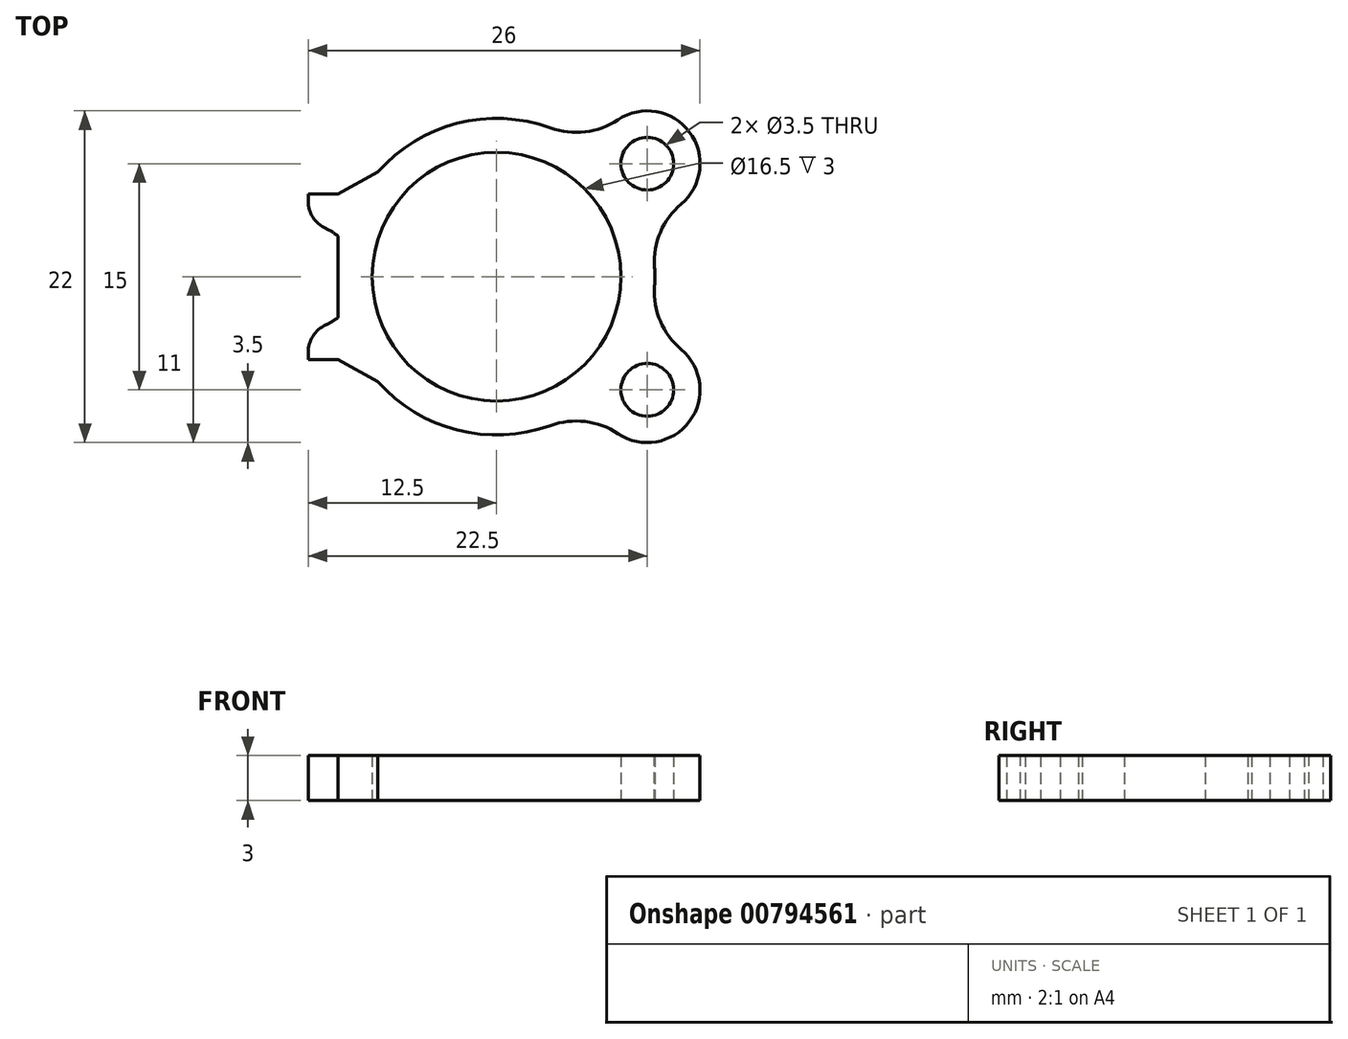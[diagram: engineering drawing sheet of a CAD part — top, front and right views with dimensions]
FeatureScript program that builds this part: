
annotation { "Feature Type Name" : "Feature", "Feature Type Description" : "" }
export const myFeature = defineFeature(function(context is Context, id is Id, definition is map)
    precondition{}
    {
        {
            var Q0;
            Q0=qCreatedBy(makeId("Top.planeOp"),FACE);
            var sketch = newSketch(context, id + "F0", { "sketchPlane" : qUnion([Q0])});
            skCircle(sketch, "E0", {"center": v(0, 0) * mm, "radius": 10.5 * mm});
            skCircle(sketch, "E1", {"center": v(0, 0) * mm, "radius": 8.25 * mm});
            skCircle(sketch, "E2", {"center": v(10, 7.5) * mm, "radius": 1.75 * mm});
            skCircle(sketch, "E3", {"center": v(10, -7.5) * mm, "radius": 1.75 * mm});
            skCircle(sketch, "E4", {"center": v(10, 7.5) * mm, "radius": 3.5 * mm});
            skCircle(sketch, "E5", {"center": v(10, -7.5) * mm, "radius": 3.5 * mm});
            skLineSegment(sketch, "E6", {"start": v(-12.5, 5.5) * mm, "end": v(-12.5, -5.5) * mm});
            skLineSegment(sketch, "E7", {"start": v(-12.5, -5.5) * mm, "end": v(-10.5, -5.5) * mm});
            skLineSegment(sketch, "E8", {"start": v(-12.5, 5.5) * mm, "end": v(-10.5, 5.5) * mm});
            skLineSegment(sketch, "E9", {"start": v(-10.5, 5.5) * mm, "end": v(-10.5, -5.5) * mm});
            skLineSegment(sketch, "E10", {"start": v(-10.5, 5.5) * mm, "end": v(-7.87, 6.95) * mm});
            skLineSegment(sketch, "E11", {"start": v(-10.5, -5.5) * mm, "end": v(-7.87, -6.95) * mm});
            skCircle(sketch, "E12", {"center": v(0, 0) * mm, "radius": 9.25 * mm});
            skLineSegment(sketch, "E13", {"start": v(-7.87, 6.95) * mm, "end": v(-7.23, 5.77) * mm});
            skLineSegment(sketch, "E14", {"start": v(-7.87, -6.95) * mm, "end": v(-7.23, -5.77) * mm});
            skCircle(sketch, "E15", {"center": v(-12.75, 0) * mm, "radius": 1.75 * mm});
            skCircle(sketch, "E16", {"center": v(-12.75, 0) * mm, "radius": 3.5 * mm});
            skSolve(sketch);
        }
        {
            var Q0;
            {var subQ2=sQuery(id+"F0.wireOp",EDGE,"E16");var subQ5=sQuery(id+"F0.wireOp",EDGE,"E6");var subQ9=makeQuery(id+"F0.imprint","INTERSECT",VERTEX,{"disambiguationData":[OD(0.0)],"derivedFrom":[subQ5,subQ2]});Q0=makeQuery(id+"F0.imprint","IMPRINT",FACE,{"disambiguationData":[TD([[makeQuery(id+"F0.imprint","IMPRINT",EDGE,{"disambiguationData":[TD([[subQ9,-1.0]])],"derivedFrom":subQ5}),1.0]])]});}
            var Q1;
            {var subQ0=sQuery(id+"F0.wireOp",EDGE,"E16");var subQ1=sQuery(id+"F0.wireOp",EDGE,"E6");var subQ2=makeQuery(id+"F0.imprint","INTERSECT",VERTEX,{"disambiguationData":[OD(0.0)],"derivedFrom":[subQ1,subQ0]});Q1=makeQuery(id+"F0.imprint","IMPRINT",FACE,{"disambiguationData":[TD([[makeQuery(id+"F0.imprint","IMPRINT",EDGE,{"disambiguationData":[TD([[subQ2,-1.0]])],"derivedFrom":subQ1}),-1.0]])]});}
            var Q2;
            {var subQ0=sQuery(id+"F0.wireOp",EDGE,"E8");Q2=makeQuery(id+"F0.imprint","IMPRINT",FACE,{"disambiguationData":[TD([[makeQuery(id+"F0.imprint","IMPRINT",EDGE,{"derivedFrom":subQ0}),-1.0]])]});}
            var Q3;
            {var subQ0=sQuery(id+"F0.wireOp",EDGE,"E10");Q3=makeQuery(id+"F0.imprint","IMPRINT",FACE,{"disambiguationData":[TD([[makeQuery(id+"F0.imprint","IMPRINT",EDGE,{"derivedFrom":subQ0}),-1.0]])]});}
            var Q4;
            {var subQ0=sQuery(id+"F0.wireOp",EDGE,"E13");Q4=makeQuery(id+"F0.imprint","IMPRINT",FACE,{"disambiguationData":[TD([[makeQuery(id+"F0.imprint","IMPRINT",EDGE,{"derivedFrom":subQ0}),-1.0]])]});}
            var Q5;
            {var subQ0=sQuery(id+"F0.wireOp",EDGE,"E13");Q5=makeQuery(id+"F0.imprint","IMPRINT",FACE,{"disambiguationData":[TD([[makeQuery(id+"F0.imprint","IMPRINT",EDGE,{"derivedFrom":subQ0}),1.0]])]});}
            var Q6;
            Q6=makeQuery(id+"F0.imprint","IMPRINT",FACE,{"disambiguationData":[TD([[makeQuery(id+"F0.imprint","IMPRINT",EDGE,{"derivedFrom":sQuery(id+"F0.wireOp",EDGE,"E1")}),-1.0]])]});
            var Q7;
            {var subQ0=sQuery(id+"F0.wireOp",EDGE,"E7");Q7=makeQuery(id+"F0.imprint","IMPRINT",FACE,{"disambiguationData":[TD([[makeQuery(id+"F0.imprint","IMPRINT",EDGE,{"derivedFrom":subQ0}),1.0]])]});}
            var Q8;
            {var subQ0=sQuery(id+"F0.wireOp",EDGE,"E11");Q8=makeQuery(id+"F0.imprint","IMPRINT",FACE,{"disambiguationData":[TD([[makeQuery(id+"F0.imprint","IMPRINT",EDGE,{"derivedFrom":subQ0}),1.0]])]});}
            var Q9;
            {var subQ0=sQuery(id+"F0.wireOp",EDGE,"E9");var subQ1=sQuery(id+"F0.wireOp",EDGE,"E0");var subQ2=makeQuery(id+"F0.imprint","INTERSECT",VERTEX,{"derivedFrom":[subQ1,subQ0]});Q9=makeQuery(id+"F0.imprint","IMPRINT",FACE,{"disambiguationData":[TD([[makeQuery(id+"F0.imprint","IMPRINT",EDGE,{"disambiguationData":[TD([[subQ2,-1.0]])],"derivedFrom":subQ1}),-1.0]])]});}
            var Q10;
            {var subQ0=sQuery(id+"F0.wireOp",EDGE,"E16");var subQ1=sQuery(id+"F0.wireOp",EDGE,"E0");var subQ2=makeQuery(id+"F0.imprint","INTERSECT",VERTEX,{"disambiguationData":[OD(0.0)],"derivedFrom":[subQ1,subQ0]});Q10=makeQuery(id+"F0.imprint","IMPRINT",FACE,{"disambiguationData":[TD([[makeQuery(id+"F0.imprint","IMPRINT",EDGE,{"disambiguationData":[TD([[subQ2,-1.0]])],"derivedFrom":subQ1}),1.0]])]});}
            var Q11;
            {var subQ0=sQuery(id+"F0.wireOp",EDGE,"E14");Q11=makeQuery(id+"F0.imprint","IMPRINT",FACE,{"disambiguationData":[TD([[makeQuery(id+"F0.imprint","IMPRINT",EDGE,{"derivedFrom":subQ0}),1.0]])]});}
            var Q12;
            {var subQ0=sQuery(id+"F0.wireOp",EDGE,"E16");var subQ1=sQuery(id+"F0.wireOp",EDGE,"E0");var subQ2=makeQuery(id+"F0.imprint","INTERSECT",VERTEX,{"disambiguationData":[OD(0.0)],"derivedFrom":[subQ1,subQ0]});Q12=makeQuery(id+"F0.imprint","IMPRINT",FACE,{"disambiguationData":[TD([[makeQuery(id+"F0.imprint","IMPRINT",EDGE,{"disambiguationData":[TD([[subQ2,-1.0]])],"derivedFrom":subQ1}),-1.0]])]});}
            var Q13;
            {var subQ0=sQuery(id+"F0.wireOp",EDGE,"E14");Q13=makeQuery(id+"F0.imprint","IMPRINT",FACE,{"disambiguationData":[TD([[makeQuery(id+"F0.imprint","IMPRINT",EDGE,{"derivedFrom":subQ0}),-1.0]])]});}
            var Q14;
            {var subQ0=sQuery(id+"F0.wireOp",EDGE,"E5");var subQ1=sQuery(id+"F0.wireOp",EDGE,"E0");var subQ9=makeQuery(id+"F0.imprint","INTERSECT",VERTEX,{"disambiguationData":[OD(0.0)],"derivedFrom":[subQ1,subQ0]});Q14=makeQuery(id+"F0.imprint","IMPRINT",FACE,{"disambiguationData":[TD([[makeQuery(id+"F0.imprint","IMPRINT",EDGE,{"disambiguationData":[TD([[subQ9,-1.0]])],"derivedFrom":subQ1}),1.0]])]});}
            var Q15;
            {var subQ0=sQuery(id+"F0.wireOp",EDGE,"E5");var subQ1=sQuery(id+"F0.wireOp",EDGE,"E0");var subQ2=makeQuery(id+"F0.imprint","INTERSECT",VERTEX,{"disambiguationData":[OD(0.0)],"derivedFrom":[subQ1,subQ0]});Q15=makeQuery(id+"F0.imprint","IMPRINT",FACE,{"disambiguationData":[TD([[makeQuery(id+"F0.imprint","IMPRINT",EDGE,{"disambiguationData":[TD([[subQ2,-1.0]])],"derivedFrom":subQ1}),-1.0]])]});}
            var Q16;
            {var subQ0=sQuery(id+"F0.wireOp",EDGE,"E12");var subQ1=sQuery(id+"F0.wireOp",EDGE,"E5");var subQ2=makeQuery(id+"F0.imprint","INTERSECT",VERTEX,{"disambiguationData":[OD(0.0)],"derivedFrom":[subQ1,subQ0]});Q16=makeQuery(id+"F0.imprint","IMPRINT",FACE,{"disambiguationData":[TD([[makeQuery(id+"F0.imprint","IMPRINT",EDGE,{"disambiguationData":[TD([[subQ2,-1.0]])],"derivedFrom":subQ1}),1.0]])]});}
            var Q17;
            {var subQ0=sQuery(id+"F0.wireOp",EDGE,"E4");var subQ1=sQuery(id+"F0.wireOp",EDGE,"E0");var subQ2=makeQuery(id+"F0.imprint","INTERSECT",VERTEX,{"disambiguationData":[OD(0.0)],"derivedFrom":[subQ1,subQ0]});Q17=makeQuery(id+"F0.imprint","IMPRINT",FACE,{"disambiguationData":[TD([[makeQuery(id+"F0.imprint","IMPRINT",EDGE,{"disambiguationData":[TD([[subQ2,1.0]])],"derivedFrom":subQ1}),1.0]])]});}
            var Q18;
            {var subQ0=sQuery(id+"F0.wireOp",EDGE,"E12");var subQ1=sQuery(id+"F0.wireOp",EDGE,"E4");var subQ2=makeQuery(id+"F0.imprint","INTERSECT",VERTEX,{"disambiguationData":[OD(0.0)],"derivedFrom":[subQ1,subQ0]});Q18=makeQuery(id+"F0.imprint","IMPRINT",FACE,{"disambiguationData":[TD([[makeQuery(id+"F0.imprint","IMPRINT",EDGE,{"disambiguationData":[TD([[subQ2,-1.0]])],"derivedFrom":subQ1}),1.0]])]});}
            var Q19;
            {var subQ0=sQuery(id+"F0.wireOp",EDGE,"E4");var subQ1=sQuery(id+"F0.wireOp",EDGE,"E0");var subQ8=makeQuery(id+"F0.imprint","INTERSECT",VERTEX,{"disambiguationData":[OD(0.0)],"derivedFrom":[subQ1,subQ0]});Q19=makeQuery(id+"F0.imprint","IMPRINT",FACE,{"disambiguationData":[TD([[makeQuery(id+"F0.imprint","IMPRINT",EDGE,{"disambiguationData":[TD([[subQ8,-1.0]])],"derivedFrom":subQ1}),1.0]])]});}
            var Q20;
            {var subQ0=sQuery(id+"F0.wireOp",EDGE,"E4");var subQ1=sQuery(id+"F0.wireOp",EDGE,"E0");var subQ2=makeQuery(id+"F0.imprint","INTERSECT",VERTEX,{"disambiguationData":[OD(0.0)],"derivedFrom":[subQ1,subQ0]});Q20=makeQuery(id+"F0.imprint","IMPRINT",FACE,{"disambiguationData":[TD([[makeQuery(id+"F0.imprint","IMPRINT",EDGE,{"disambiguationData":[TD([[subQ2,-1.0]])],"derivedFrom":subQ1}),-1.0]])]});}
            var Q21;
            {var subQ1=sQuery(id+"F0.wireOp",EDGE,"E1");var subQ6=sQuery(id+"F0.wireOp",EDGE,"E4");var subQ8=makeQuery(id+"F0.imprint","INTERSECT",VERTEX,{"disambiguationData":[OD(0.0)],"derivedFrom":[subQ1,subQ6]});Q21=makeQuery(id+"F0.imprint","IMPRINT",FACE,{"disambiguationData":[TD([[makeQuery(id+"F0.imprint","IMPRINT",EDGE,{"disambiguationData":[TD([[subQ8,-1.0]])],"derivedFrom":subQ1}),-1.0]])]});}
            var Q22;
            {var subQ0=sQuery(id+"F0.wireOp",EDGE,"E4");var subQ1=sQuery(id+"F0.wireOp",EDGE,"E0");var subQ2=makeQuery(id+"F0.imprint","INTERSECT",VERTEX,{"disambiguationData":[OD(1.0)],"derivedFrom":[subQ1,subQ0]});Q22=makeQuery(id+"F0.imprint","IMPRINT",FACE,{"disambiguationData":[TD([[makeQuery(id+"F0.imprint","IMPRINT",EDGE,{"disambiguationData":[TD([[subQ2,1.0]])],"derivedFrom":subQ1}),1.0]])]});}
            var Q23;
            Q23=makeQuery(id+"F0.imprint","IMPRINT",FACE,{"disambiguationData":[TD([[makeQuery(id+"F0.imprint","IMPRINT",EDGE,{"derivedFrom":sQuery(id+"F0.wireOp",EDGE,"E2")}),-1.0]])]});
            extrude(context, id + "F1", {"entities" : qUnion([Q0, Q1, Q2, Q3, Q4, Q5, Q6, Q7, Q8, Q9, Q10, Q11, Q12, Q13, Q14, Q15, Q16, Q17, Q18, Q19, Q20, Q21, Q22, Q23]), "depth" : 3 * mm, "offsetDistance" : 25 * mm});
        }
        {
            var Q0;
            {var subQ0=sQuery(id+"F0.wireOp",EDGE,"E16");var subQ1=sQuery(id+"F0.wireOp",EDGE,"E6");Q0=makeQuery(id+"F1.opExtrude","SWEPT_EDGE",EDGE,{"disambiguationData":[OSD([subQ1,subQ0]),TDD([makeQuery(id+"F0.imprint","INTERSECT",VERTEX,{"disambiguationData":[OD(1.0)],"derivedFrom":[subQ1,subQ0]})])]});}
            var Q1;
            {var subQ0=sQuery(id+"F0.wireOp",EDGE,"E16");var subQ1=sQuery(id+"F0.wireOp",EDGE,"E6");Q1=makeQuery(id+"F1.opExtrude","SWEPT_EDGE",EDGE,{"disambiguationData":[OSD([subQ1,subQ0]),TDD([makeQuery(id+"F0.imprint","INTERSECT",VERTEX,{"disambiguationData":[OD(0.0)],"derivedFrom":[subQ1,subQ0]})])]});}
            fillet(context, id + "F2", {"entities" : qUnion([Q0, Q1]), "radius" : 2 * mm, "tangentPropagation" : true, "allowEdgeOverflow" : false});
        }
        {
            var Q0;
            {var subQ0=sQuery(id+"F0.wireOp",EDGE,"E5");var subQ1=sQuery(id+"F0.wireOp",EDGE,"E0");Q0=makeQuery(id+"F1.opExtrude","SWEPT_EDGE",EDGE,{"disambiguationData":[OSD([subQ1,subQ0]),TDD([makeQuery(id+"F0.imprint","INTERSECT",VERTEX,{"disambiguationData":[OD(0.0)],"derivedFrom":[subQ1,subQ0]})])]});}
            var Q1;
            {var subQ0=sQuery(id+"F0.wireOp",EDGE,"E5");var subQ1=sQuery(id+"F0.wireOp",EDGE,"E0");Q1=makeQuery(id+"F1.opExtrude","SWEPT_EDGE",EDGE,{"disambiguationData":[OSD([subQ1,subQ0]),TDD([makeQuery(id+"F0.imprint","INTERSECT",VERTEX,{"disambiguationData":[OD(1.0)],"derivedFrom":[subQ1,subQ0]})])]});}
            var Q2;
            {var subQ0=sQuery(id+"F0.wireOp",EDGE,"E4");var subQ1=sQuery(id+"F0.wireOp",EDGE,"E0");Q2=makeQuery(id+"F1.opExtrude","SWEPT_EDGE",EDGE,{"disambiguationData":[OSD([subQ1,subQ0]),TDD([makeQuery(id+"F0.imprint","INTERSECT",VERTEX,{"disambiguationData":[OD(0.0)],"derivedFrom":[subQ1,subQ0]})])]});}
            var Q3;
            {var subQ0=sQuery(id+"F0.wireOp",EDGE,"E4");var subQ1=sQuery(id+"F0.wireOp",EDGE,"E0");Q3=makeQuery(id+"F1.opExtrude","SWEPT_EDGE",EDGE,{"disambiguationData":[OSD([subQ1,subQ0]),TDD([makeQuery(id+"F0.imprint","INTERSECT",VERTEX,{"disambiguationData":[OD(1.0)],"derivedFrom":[subQ1,subQ0]})])]});}
            fillet(context, id + "F3", {"entities" : qUnion([Q0, Q1, Q2, Q3]), "radius" : 5 * mm, "tangentPropagation" : true, "allowEdgeOverflow" : false});
        }
    });
